# Revit family: Keilhauer_Pact_Table_77432
name_source: partatom
category: Furniture
revit_build: Autodesk Revit 2017 (Build: 20160225_1515(x64)
units: mm (PartAtom-declared; Revit-internal decimal feet)

## family parameters
Always vertical = Yes
Cut with Voids When Loaded = No
OmniClass Number = 23.40.70.14.64.11
OmniClass Title = Office Furniture
Room Calculation Point = No
Shared = No
Work Plane-Based = No

## types (3) — shared parameters
Assembly Code = E2020200
Catalog = Pact
Manufacturer = Keilhauer, Corp.
Product Documentation Link = http://www.keilhauer.com
URL = http://www.keilhauer.com

## per-type parameters (varying)
| type | Base 1 | Base 2 | Description | Length | Model | Type |
| 56 x 32 rectangular | No | Yes | 56 x 32 rectangular conference table | 28 " | 77434 | 3 |
| 28 x 32 square | Yes | No | 28 x 32 square conference table | 14 " | 77433 | 2 |
| 24 x 32 rectangular | Yes | No | 24 x 32 rectangular conference table | 12 " | 77432 | 1 |

## geometry (parser evidence)
native form markers: Sweep x5
no freeform markers — native parametric forms only
